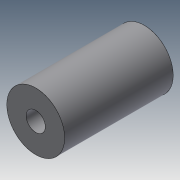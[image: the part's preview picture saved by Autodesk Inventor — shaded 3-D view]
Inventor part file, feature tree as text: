
AUTODESK INVENTOR PART (.ipt)
format: ipt  version: 2018.3 (Build 223284000, 284)  size: 103,424 bytes
history: native  units: in
note: dims shown in document units (in); Inventor stores cm internally (conversion verified against a paired STEP export)
features: extrude x1
ambient origin geometry x8: Origin, YZ Plane, XZ Plane, XY Plane, X Axis, Y Axis, Z Axis, Center Point
bodies: Solid1 (feature_tree)
feature tree (1):
  extrude  "Extrude1"  [1 undecoded]
note: 1 required parameter value undecoded (feature->parameter linkage not recoverable at this tier; creation-order binding heuristic only, values carry confidence <= 0.55)
